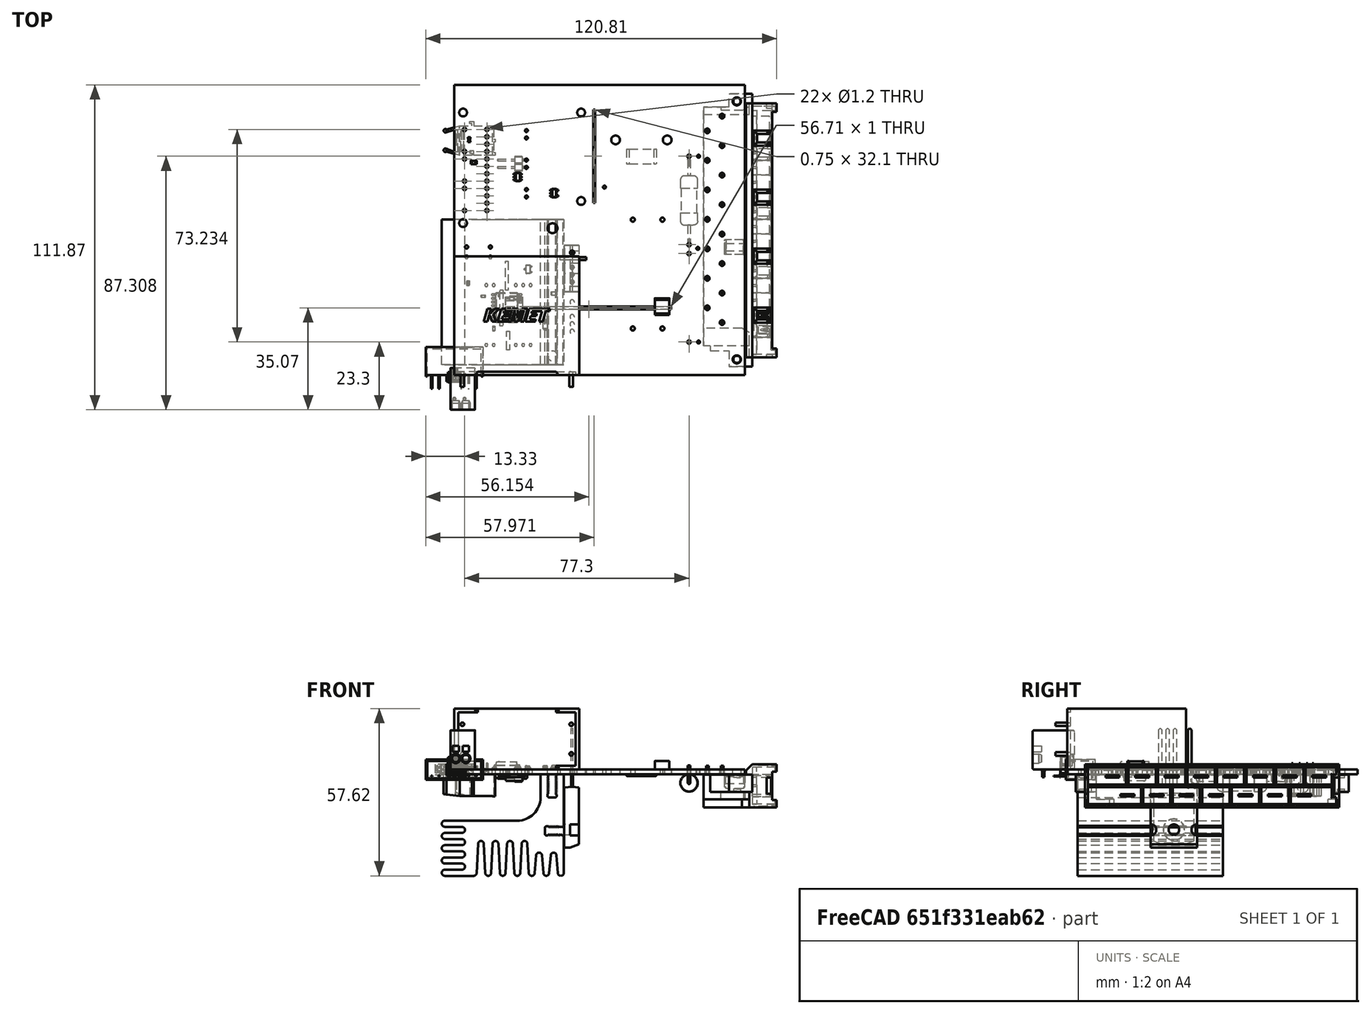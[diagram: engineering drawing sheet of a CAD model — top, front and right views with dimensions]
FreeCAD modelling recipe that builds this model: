
FCSTD DOCUMENT  (FreeCAD 1.0R39109 (Git))
Label: HalfBridge_SiC
License: All rights reserved
LicenseURL: https://en.wikipedia.org/wiki/All_rights_reserved
objects: App::Link×105, Part::Feature×46, App::Part×15, PartDesign::CoordinateSystem×1, Sketcher::SketchObject×1
note: 49 computed .brp shape members not serialized (recipe doc carries the construction recipe); baked Part::Feature solids carry a one-line shape summary decoded from their .brp

FEATURE [PartDesign::CoordinateSystem] Local_CS_ed05
  AttacherType = Attacher::AttachEngine3D
  MapMode = 2
FEATURE [Part::Feature] Pcb_ed05
  Placement = pos=(-39.5,140.5,0) rot=(0,0,1;0rad)
  shape: bbox 100 x 100 x 1.6 mm, 113 faces (baked)
FEATURE [Sketcher::SketchObject] PCB_Sketch_ed05
  ArcFitTolerance = 1e-06
  FullyConstrained = false
  MakeInternals = false
  sketch-geometry (28):
    g0: LineSegment StartX=17.542 StartY=39.29 StartZ=0 EndX=18.542 EndY=39.29 EndZ=0
    g1: LineSegment StartX=18.542 StartY=39.29 StartZ=0 EndX=18.542 EndY=29.29 EndZ=0
    g2: LineSegment StartX=18.542 StartY=29.29 StartZ=0 EndX=17.542 EndY=29.29 EndZ=0
    g3: LineSegment StartX=17.542 StartY=29.29 StartZ=0 EndX=17.542 EndY=39.29 EndZ=0
    g4: LineSegment StartX=36.399 StartY=40.662 StartZ=0 EndX=45.383 EndY=40.662 EndZ=0
    g5: LineSegment StartX=45.383 StartY=40.662 StartZ=0 EndX=45.383 EndY=39.662 EndZ=0
    g6: LineSegment StartX=45.383 StartY=39.662 StartZ=0 EndX=36.399 EndY=39.662 EndZ=0
    g7: LineSegment StartX=36.399 StartY=39.662 StartZ=0 EndX=36.399 EndY=40.662 EndZ=0
    g8: LineSegment StartX=47.768 StartY=91.487 StartZ=0 EndX=48.514 EndY=91.487 EndZ=0
    g9: LineSegment StartX=48.514 StartY=91.487 StartZ=0 EndX=48.514 EndY=59.389 EndZ=0
    g10: LineSegment StartX=48.514 StartY=59.389 StartZ=0 EndX=47.768 EndY=59.389 EndZ=0
    g11: LineSegment StartX=47.768 StartY=59.389 StartZ=0 EndX=47.768 EndY=91.487 EndZ=0
    g12: LineSegment StartX=17.968 StartY=23.7 StartZ=0 EndX=74.68 EndY=23.7 EndZ=0
    g13: LineSegment StartX=74.68 StartY=23.7 StartZ=0 EndX=74.68 EndY=22.7 EndZ=0
    g14: LineSegment StartX=74.68 StartY=22.7 StartZ=0 EndX=17.968 EndY=22.7 EndZ=0
    g15: LineSegment StartX=17.968 StartY=22.7 StartZ=0 EndX=17.968 EndY=23.7 EndZ=0
    g16: LineSegment StartX=0 StartY=100 StartZ=0 EndX=100 EndY=100 EndZ=0
    g17: LineSegment StartX=100 StartY=100 StartZ=0 EndX=100 EndY=0 EndZ=0
    g18: LineSegment StartX=100 StartY=0 StartZ=0 EndX=0 EndY=0 EndZ=0
    g19: LineSegment StartX=0 StartY=0 StartZ=0 EndX=0 EndY=100 EndZ=0
    g20: LineSegment StartX=18.05 StartY=15.208 StartZ=0 EndX=19.05 EndY=15.208 EndZ=0
    g21: LineSegment StartX=19.05 StartY=15.208 StartZ=0 EndX=19.05 EndY=8.7 EndZ=0
    g22: LineSegment StartX=19.05 StartY=8.7 StartZ=0 EndX=18.05 EndY=8.7 EndZ=0
    g23: LineSegment StartX=18.05 StartY=8.7 StartZ=0 EndX=18.05 EndY=15.208 EndZ=0
    g24: LineSegment StartX=15.764 StartY=29.4 StartZ=0 EndX=16.764 EndY=29.4 EndZ=0
    g25: LineSegment StartX=16.764 StartY=29.4 StartZ=0 EndX=16.764 EndY=16.9 EndZ=0
    g26: LineSegment StartX=16.764 StartY=16.9 StartZ=0 EndX=15.764 EndY=16.9 EndZ=0
    g27: LineSegment StartX=15.764 StartY=16.9 StartZ=0 EndX=15.764 EndY=29.4 EndZ=0
  constraints (28):
    c: Coincident(g18,g19)
    c: Coincident(g16,g19)
    c: Coincident(g26,g27)
    c: Coincident(g24,g27)
    c: Coincident(g25,g26)
    c: Coincident(g24,g25)
    c: Coincident(g2,g3)
    c: Coincident(g0,g3)
    c: Coincident(g14,g15)
    c: Coincident(g12,g15)
    c: Coincident(g22,g23)
    c: Coincident(g20,g23)
    c: Coincident(g1,g2)
    c: Coincident(g0,g1)
    c: Coincident(g21,g22)
    c: Coincident(g20,g21)
    c: Coincident(g6,g7)
    c: Coincident(g4,g7)
    c: Coincident(g5,g6)
    c: Coincident(g4,g5)
    c: Coincident(g10,g11)
    c: Coincident(g8,g11)
    c: Coincident(g9,g10)
    c: Coincident(g8,g9)
    c: Coincident(g13,g14)
    c: Coincident(g12,g13)
    c: Coincident(g17,g18)
    c: Coincident(g16,g17)
FEATURE [App::Part] Board_Geoms_ed05
  Group = -> [Pcb_ed05,PCB_Sketch_ed05]
  Origin = -> Origin
FEATURE [Part::Feature] Shape  label="U5_SOIC-16W_7.5x10.3mm_P1.27mm_noPin12_13_606f1c37d418"
  Placement = pos=(18,23.3,0) rot=(0,0,1;0rad)
  shape: bbox 10.3 x 10.3 x 2.75 mm, 256 faces (baked)
FEATURE [Part::Feature] Shape001  label="D6_D_SOD_123_86f777a7cf57"
  Placement = pos=(31.3,17.35,0) rot=(0,0,-1;1.5708rad)
  shape: bbox 1.6 x 3.8 x 1.25 mm, 67 faces (baked)
FEATURE [Part::Feature] Shape002  label="R9_R_0603_1608Metric_fe9d9f34c5f9"
  Placement = pos=(9.9875,27.2,0) rot=(0,0,1;0rad)
  shape: bbox 1.6 x 0.8 x 0.45 mm, 26 faces (baked)
FEATURE [App::Link] D6_D_SOD_123_86f777a7cf57_ln_  label="D5_D_SOD_123_75c73be4f775"
  LinkPlacement = pos=(31.3,29.9,0) rot=(0,0,1;1.5708rad)
  LinkedObject = -> Shape001
  Placement = pos=(31.3,29.9,0) rot=(0,0,1;1.5708rad)
FEATURE [Part::Feature] Shape003  label="C15_C_0603_1608Metric_09ddd0478757"
  Placement = pos=(13.5,16.1,0) rot=(0,0,-1;1.5708rad)
  shape: bbox 0.8 x 1.6 x 0.8 mm, 28 faces (baked)
FEATURE [App::Link] C15_C_0603_1608Metric_09ddd0478757_ln_  label="C33_C_0603_1608Metric_74bc470caa33"
  LinkPlacement = pos=(9.3,80.8715,0) rot=(0,0,1;1.5708rad)
  LinkedObject = -> Shape003
  Placement = pos=(9.3,80.8715,0) rot=(0,0,1;1.5708rad)
FEATURE [Part::Feature] Shape004  label="D3_LED_0603_1608Metric_70bb5031e2ff"
  Placement = pos=(4.7,31.775,0) rot=(0,0,-1;1.5708rad)
  shape: bbox 0.8 x 1.6 x 1.1 mm, 50 faces (baked)
FEATURE [Part::Feature] Shape005  label="C38_C_0805_2012Metric_74cbd35bff10"
  Placement = pos=(6.655,73.284,0) rot=(0,0,1;0rad)
  shape: bbox 2 x 1.25 x 1.25 mm, 28 faces (baked)
FEATURE [App::Link] R9_R_0603_1608Metric_fe9d9f34c5f9_ln_  label="R33_R_0603_1608Metric_ea8747869db3"
  LinkPlacement = pos=(22.7,83.4115,0) rot=(0,0,1;1.5708rad)
  LinkedObject = -> Shape002
  Placement = pos=(22.7,83.4115,0) rot=(0,0,1;1.5708rad)
FEATURE [App::Link] C15_C_0603_1608Metric_09ddd0478757_ln_001  label="C22_C_0603_1608Metric_3b7886544036"
  LinkPlacement = pos=(25.65,28.3,0) rot=(0,0,1;0rad)
  LinkedObject = -> Shape003
  Placement = pos=(25.65,28.3,0) rot=(0,0,1;0rad)
FEATURE [Part::Feature] Part__Feature  label="CAS_c_12B"
  Placement = pos=(0,-2.4,-3e-16) rot=(0,0,1;0rad)
  shape: bbox 5.4 x 2.5 x 4.2 mm, 71 faces (baked)
FEATURE [Part::Feature] Part__Feature001  label="1 pole_s"
  Placement = pos=(0.3,-0.6,-3e-16) rot=(0,0,1;0rad)
  shape: bbox 0.6 x 0.6 x 0.7 mm, 14 faces (baked)
FEATURE [App::Part] CAS_120B1  label="SW1_CAS-120B1_eba1f44a47b7[2]"
  Group = -> [Part__Feature,Part__Feature001]
  Origin = -> Origin008
  Placement = pos=(29.242,83.058,2.5) rot=(0.57735,-0.57735,-0.57735;2.0944rad)
FEATURE [App::Link] R9_R_0603_1608Metric_fe9d9f34c5f9_ln_001  label="R14_R_0603_1608Metric_f9b5c031c635"
  LinkPlacement = pos=(28.1,36.5,0) rot=(0,0,1;1.5708rad)
  LinkedObject = -> Shape002
  Placement = pos=(28.1,36.5,0) rot=(0,0,1;1.5708rad)
FEATURE [App::Link] R9_R_0603_1608Metric_fe9d9f34c5f9_ln_002  label="R8_R_0603_1608Metric_fcb6b5fbbfd0"
  LinkPlacement = pos=(10,28.7,0) rot=(0,0,1;0rad)
  LinkedObject = -> Shape002
  Placement = pos=(10,28.7,0) rot=(0,0,1;0rad)
FEATURE [App::Link] C15_C_0603_1608Metric_09ddd0478757_ln_002  label="C45_C_0603_1608Metric_6c9f5762c5a1"
  LinkPlacement = pos=(36.9,16.256,0) rot=(0,0,1;1.5708rad)
  LinkedObject = -> Shape003
  Placement = pos=(36.9,16.256,0) rot=(0,0,1;1.5708rad)
FEATURE [App::Link] C38_C_0805_2012Metric_74cbd35bff10_ln_  label="C24_C_0805_2012Metric_4c91d95a9eef"
  LinkPlacement = pos=(25.7,8.7,0) rot=(0,0,1;3.14159rad)
  LinkedObject = -> Shape005
  Placement = pos=(25.7,8.7,0) rot=(0,0,1;3.14159rad)
FEATURE [Part::Feature] Shape006  label="U10_SOT_23_6_8cf1dc40b667"
  Placement = pos=(21.85,68.3115,0) rot=(0,0,1;3.14159rad)
  shape: bbox 2.8 x 2.9 x 1.55 mm, 124 faces (baked)
FEATURE [App::Link] C15_C_0603_1608Metric_09ddd0478757_ln_003  label="C21_C_0603_1608Metric_d16c1e161e8d"
  LinkPlacement = pos=(25.62,18.5,0) rot=(0,0,1;3.14159rad)
  LinkedObject = -> Shape003
  Placement = pos=(25.62,18.5,0) rot=(0,0,1;3.14159rad)
FEATURE [App::Link] C15_C_0603_1608Metric_09ddd0478757_ln_004  label="C42_C_0603_1608Metric_20bf4b114d9d"
  LinkPlacement = pos=(25.1,68.1115,0) rot=(0,0,1;1.5708rad)
  LinkedObject = -> Shape003
  Placement = pos=(25.1,68.1115,0) rot=(0,0,1;1.5708rad)
FEATURE [App::Link] C38_C_0805_2012Metric_74cbd35bff10_ln_001  label="C18_C_0805_2012Metric_4df3bd6c3c50"
  LinkPlacement = pos=(25.7,33.1,0) rot=(0,0,1;3.14159rad)
  LinkedObject = -> Shape005
  Placement = pos=(25.7,33.1,0) rot=(0,0,1;3.14159rad)
FEATURE [App::Link] U10_SOT_23_6_8cf1dc40b667_ln_  label="U11_SOT_23_6_c211cb7acc4a"
  LinkPlacement = pos=(21.85,58.1515,0) rot=(0,0,1;3.14159rad)
  LinkedObject = -> Shape006
  Placement = pos=(21.85,58.1515,0) rot=(0,0,1;3.14159rad)
FEATURE [App::Link] R9_R_0603_1608Metric_fe9d9f34c5f9_ln_003  label="R15_R_0603_1608Metric_55e85660f00f"
  LinkPlacement = pos=(22.6,36.1,0) rot=(0,0,-1;1.5708rad)
  LinkedObject = -> Shape002
  Placement = pos=(22.6,36.1,0) rot=(0,0,-1;1.5708rad)
FEATURE [Part::Feature] Shape007  label="R21_R_0805_2012Metric_4eff570911b6"
  Placement = pos=(34.3,28.2,0) rot=(0,0,1;0rad)
  shape: bbox 2 x 1.2 x 0.45 mm, 26 faces (baked)
FEATURE [App::Link] C15_C_0603_1608Metric_09ddd0478757_ln_005  label="C34_C_0603_1608Metric_836b7f75df63"
  LinkPlacement = pos=(9.5,60.3715,0) rot=(0,0,1;1.5708rad)
  LinkedObject = -> Shape003
  Placement = pos=(9.5,60.3715,0) rot=(0,0,1;1.5708rad)
FEATURE [App::Link] C38_C_0805_2012Metric_74cbd35bff10_ln_002  label="C39_C_0805_2012Metric_4739b33e3560"
  LinkPlacement = pos=(6.655,83.9115,0) rot=(0,0,1;0rad)
  LinkedObject = -> Shape005
  Placement = pos=(6.655,83.9115,0) rot=(0,0,1;0rad)
FEATURE [App::Link] R9_R_0603_1608Metric_fe9d9f34c5f9_ln_004  label="R16_R_0603_1608Metric_5e29ad9bbd6c"
  LinkPlacement = pos=(29.7,13.3,0) rot=(0,0,-1;1.5708rad)
  LinkedObject = -> Shape002
  Placement = pos=(29.7,13.3,0) rot=(0,0,-1;1.5708rad)
FEATURE [App::Link] C15_C_0603_1608Metric_09ddd0478757_ln_006  label="C6_C_0603_1608Metric_47ec0beeeb7c"
  LinkPlacement = pos=(36.576,85.598,0) rot=(0,0,1;0rad)
  LinkedObject = -> Shape003
  Placement = pos=(36.576,85.598,0) rot=(0,0,1;0rad)
FEATURE [App::Link] D3_LED_0603_1608Metric_70bb5031e2ff_ln_  label="D1_LED_0603_1608Metric_117d22e4d741"
  LinkPlacement = pos=(3.1,9.525,0) rot=(0,0,1;1.5708rad)
  LinkedObject = -> Shape004
  Placement = pos=(3.1,9.525,0) rot=(0,0,1;1.5708rad)
FEATURE [Part::Feature] Shape008  label="U3_SOT_23_5_e32904241429"
  Placement = pos=(34.37,62.7015,0) rot=(0,0,1;0rad)
  shape: bbox 2.8 x 2.9 x 1.55 mm, 109 faces (baked)
FEATURE [App::Link] C38_C_0805_2012Metric_74cbd35bff10_ln_003  label="C35_C_0805_2012Metric_12818f10c88b"
  LinkPlacement = pos=(7.5,67.9115,0) rot=(0,0,1;3.14159rad)
  LinkedObject = -> Shape005
  Placement = pos=(7.5,67.9115,0) rot=(0,0,1;3.14159rad)
FEATURE [Part::Feature] Shape009  label="U7_SOT_23_ed8fd63cd947"
  Placement = pos=(25.3625,36.5,0) rot=(0,0,1;3.14159rad)
  shape: bbox 2.5 x 3 x 1.2 mm, 76 faces (baked)
FEATURE [Part::Feature] Shape010  label="C5_C_2220_5750Metric_40789e461117"
  Placement = pos=(71.498,23.622,0) rot=(0,0,-1;1.5708rad)
  shape: bbox 5 x 5.7 x 2.9 mm, 28 faces (baked)
FEATURE [App::Link] R9_R_0603_1608Metric_fe9d9f34c5f9_ln_005  label="R29_R_0603_1608Metric_c415b56a8a35"
  LinkPlacement = pos=(13.655,63.4115,0) rot=(0,0,1;1.5708rad)
  LinkedObject = -> Shape002
  Placement = pos=(13.655,63.4115,0) rot=(0,0,1;1.5708rad)
FEATURE [App::Link] R9_R_0603_1608Metric_fe9d9f34c5f9_ln_006  label="R27_R_0603_1608Metric_6ecdd8c441b3"
  LinkPlacement = pos=(13.3,73.9115,0) rot=(0,0,1;1.5708rad)
  LinkedObject = -> Shape002
  Placement = pos=(13.3,73.9115,0) rot=(0,0,1;1.5708rad)
FEATURE [App::Link] R9_R_0603_1608Metric_fe9d9f34c5f9_ln_007  label="R30_R_0603_1608Metric_3d9fcfb98980"
  LinkPlacement = pos=(18.7,78.4115,0) rot=(0,0,1;1.5708rad)
  LinkedObject = -> Shape002
  Placement = pos=(18.7,78.4115,0) rot=(0,0,1;1.5708rad)
FEATURE [App::Link] C15_C_0603_1608Metric_09ddd0478757_ln_007  label="C41_C_0603_1608Metric_8a3fc6cb6ce4"
  LinkPlacement = pos=(25.1,78.4115,0) rot=(0,0,1;1.5708rad)
  LinkedObject = -> Shape003
  Placement = pos=(25.1,78.4115,0) rot=(0,0,1;1.5708rad)
FEATURE [App::Link] C5_C_2220_5750Metric_40789e461117_ln_  label="C3_C_2220_5750Metric_0b14797a19db"
  LinkPlacement = pos=(59.498,23.622,0) rot=(0,0,-1;1.5708rad)
  LinkedObject = -> Shape010
  Placement = pos=(59.498,23.622,0) rot=(0,0,-1;1.5708rad)
FEATURE [App::Link] R21_R_0805_2012Metric_4eff570911b6_ln_  label="R19_R_0805_2012Metric_5467f9f4486e"
  LinkPlacement = pos=(34.3,32.2,0) rot=(0,0,1;0rad)
  LinkedObject = -> Shape007
  Placement = pos=(34.3,32.2,0) rot=(0,0,1;0rad)
FEATURE [App::Link] C15_C_0603_1608Metric_09ddd0478757_ln_008  label="C43_C_0603_1608Metric_b35c248b52c4"
  LinkPlacement = pos=(25.1,58.1115,0) rot=(0,0,1;1.5708rad)
  LinkedObject = -> Shape003
  Placement = pos=(25.1,58.1115,0) rot=(0,0,1;1.5708rad)
FEATURE [App::Link] R21_R_0805_2012Metric_4eff570911b6_ln_001  label="R3_R_0805_2012Metric_ab16afa742b3"
  LinkPlacement = pos=(44.564,16.278,0) rot=(0,0,1;1.5708rad)
  LinkedObject = -> Shape007
  Placement = pos=(44.564,16.278,0) rot=(0,0,1;1.5708rad)
FEATURE [App::Link] R21_R_0805_2012Metric_4eff570911b6_ln_002  label="R10_R_0805_2012Metric_e1b373d5c9e0"
  LinkPlacement = pos=(8.1,18.67,0) rot=(0,0,-1;1.5708rad)
  LinkedObject = -> Shape007
  Placement = pos=(8.1,18.67,0) rot=(0,0,-1;1.5708rad)
FEATURE [App::Link] D3_LED_0603_1608Metric_70bb5031e2ff_ln_001  label="D2_LED_0603_1608Metric_72f350e39bfe"
  LinkPlacement = pos=(4.7,35.5,0) rot=(0,0,-1;1.5708rad)
  LinkedObject = -> Shape004
  Placement = pos=(4.7,35.5,0) rot=(0,0,-1;1.5708rad)
FEATURE [App::Link] R9_R_0603_1608Metric_fe9d9f34c5f9_ln_008  label="R32_R_0603_1608Metric_bd0168379d35"
  LinkPlacement = pos=(18.7,58.1115,0) rot=(0,0,1;1.5708rad)
  LinkedObject = -> Shape002
  Placement = pos=(18.7,58.1115,0) rot=(0,0,1;1.5708rad)
FEATURE [App::Link] C38_C_0805_2012Metric_74cbd35bff10_ln_004  label="C40_C_0805_2012Metric_1a8242036e69"
  LinkPlacement = pos=(6.7,63.1115,0) rot=(0,0,1;0rad)
  LinkedObject = -> Shape005
  Placement = pos=(6.7,63.1115,0) rot=(0,0,1;0rad)
FEATURE [App::Link] R21_R_0805_2012Metric_4eff570911b6_ln_003  label="R40_R_0805_2012Metric_1fb8d6502ab2"
  LinkPlacement = pos=(20.574,16.04,0) rot=(0,0,-1;1.5708rad)
  LinkedObject = -> Shape007
  Placement = pos=(20.574,16.04,0) rot=(0,0,-1;1.5708rad)
FEATURE [App::Link] C15_C_0603_1608Metric_09ddd0478757_ln_009  label="C20_C_0603_1608Metric_5de1c2e82c4e"
  LinkPlacement = pos=(25.62,21.1,0) rot=(0,0,1;0rad)
  LinkedObject = -> Shape003
  Placement = pos=(25.62,21.1,0) rot=(0,0,1;0rad)
FEATURE [App::Link] R9_R_0603_1608Metric_fe9d9f34c5f9_ln_009  label="R28_R_0603_1608Metric_db2da8ac741f"
  LinkPlacement = pos=(13.3,84.0715,0) rot=(0,0,1;1.5708rad)
  LinkedObject = -> Shape002
  Placement = pos=(13.3,84.0715,0) rot=(0,0,1;1.5708rad)
FEATURE [App::Link] C38_C_0805_2012Metric_74cbd35bff10_ln_005  label="C25_C_0805_2012Metric_d4570dd2b406"
  LinkPlacement = pos=(21.9,8.7,0) rot=(0,0,1;3.14159rad)
  LinkedObject = -> Shape005
  Placement = pos=(21.9,8.7,0) rot=(0,0,1;3.14159rad)
FEATURE [Part::Feature] Shape011  label="L5_L_0603_1608Metric_90973c27a168"
  Placement = pos=(5.1,81.1115,0) rot=(0,0,1;1.5708rad)
  shape: bbox 0.8 x 1.6 x 0.8 mm, 28 faces (baked)
FEATURE [App::Link] R21_R_0805_2012Metric_4eff570911b6_ln_004  label="R26_R_0805_2012Metric_215f856b24f5"
  LinkPlacement = pos=(34.3,13.9,0) rot=(0,0,1;0rad)
  LinkedObject = -> Shape007
  Placement = pos=(34.3,13.9,0) rot=(0,0,1;0rad)
FEATURE [App::Link] L5_L_0603_1608Metric_90973c27a168_ln_  label="L6_L_0603_1608Metric_227bb48d5cae"
  LinkPlacement = pos=(5.1,60.4265,0) rot=(0,0,1;1.5708rad)
  LinkedObject = -> Shape011
  Placement = pos=(5.1,60.4265,0) rot=(0,0,1;1.5708rad)
FEATURE [App::Link] C15_C_0603_1608Metric_09ddd0478757_ln_010  label="C14_C_0603_1608Metric_a25fa12fbfe8"
  LinkPlacement = pos=(11.3,24.6,0) rot=(0,0,-1;1.5708rad)
  LinkedObject = -> Shape003
  Placement = pos=(11.3,24.6,0) rot=(0,0,-1;1.5708rad)
FEATURE [App::Link] R9_R_0603_1608Metric_fe9d9f34c5f9_ln_010  label="R31_R_0603_1608Metric_1647f0dc400e"
  LinkPlacement = pos=(18.7,68.3115,0) rot=(0,0,1;1.5708rad)
  LinkedObject = -> Shape002
  Placement = pos=(18.7,68.3115,0) rot=(0,0,1;1.5708rad)
FEATURE [App::Link] C38_C_0805_2012Metric_74cbd35bff10_ln_006  label="C37_C_0805_2012Metric_821d07cd279f"
  LinkPlacement = pos=(7.5,57.7115,0) rot=(0,0,1;3.14159rad)
  LinkedObject = -> Shape005
  Placement = pos=(7.5,57.7115,0) rot=(0,0,1;3.14159rad)
FEATURE [App::Link] C5_C_2220_5750Metric_40789e461117_ln_001  label="C4_C_2220_5750Metric_aeb9c5b40f04"
  LinkPlacement = pos=(65.498,23.622,0) rot=(0,0,-1;1.5708rad)
  LinkedObject = -> Shape010
  Placement = pos=(65.498,23.622,0) rot=(0,0,-1;1.5708rad)
FEATURE [Part::Feature] Part__Feature002  label="CAS_c_D2B"
  Placement = pos=(0,-2.4,-3e-16) rot=(0,0,1;0rad)
  shape: bbox 5.4 x 2.5 x 5.6 mm, 110 faces (baked)
FEATURE [Part::Feature] Part__Feature003  label="Dual_s"
  Placement = pos=(0.3,-0.6,0.64) rot=(0,0,1;0rad)
  shape: bbox 0.6 x 0.6 x 0.7 mm, 14 faces (baked)
FEATURE [Part::Feature] Part__Feature004  label="Dual_s001"
  Placement = pos=(0.3,-0.6,-0.64) rot=(0,0,1;0rad)
  shape: bbox 0.6 x 0.6 x 0.7 mm, 14 faces (baked)
FEATURE [App::Part] CAS_D20B1  label="SW5_CAS-D20B1_b4c165cab9b4[2]"
  Group = -> [Part__Feature002,Part__Feature003,Part__Feature004]
  Origin = -> Origin009
  Placement = pos=(4.29,22.754,2.5) rot=(0,0.707107,0.707107;3.14159rad)
FEATURE [App::Link] R9_R_0603_1608Metric_fe9d9f34c5f9_ln_011  label="R35_R_0603_1608Metric_3c432ada0ca8"
  LinkPlacement = pos=(22.7,72.9115,0) rot=(0,0,1;1.5708rad)
  LinkedObject = -> Shape002
  Placement = pos=(22.7,72.9115,0) rot=(0,0,1;1.5708rad)
FEATURE [App::Link] U7_SOT_23_ed8fd63cd947_ln_  label="U8_SOT_23_df60fcb6f98c"
  LinkPlacement = pos=(25.3625,13.6,0) rot=(0,0,1;3.14159rad)
  LinkedObject = -> Shape009
  Placement = pos=(25.3625,13.6,0) rot=(0,0,1;3.14159rad)
FEATURE [App::Link] L5_L_0603_1608Metric_90973c27a168_ln_001  label="L4_L_0603_1608Metric_8fa15f76ae30"
  LinkPlacement = pos=(5.1,70.5865,0) rot=(0,0,1;1.5708rad)
  LinkedObject = -> Shape011
  Placement = pos=(5.1,70.5865,0) rot=(0,0,1;1.5708rad)
FEATURE [App::Link] SW1_CAS_120B1_eba1f44a47b7_2__ln_  label="SW3_CAS-120B1_d768a4589788[2]"
  LinkPlacement = pos=(29.21,62.484,2.5) rot=(0.57735,-0.57735,-0.57735;2.0944rad)
  LinkedObject = -> CAS_120B1
  Placement = pos=(29.21,62.484,2.5) rot=(0.57735,-0.57735,-0.57735;2.0944rad)
FEATURE [App::Link] C15_C_0603_1608Metric_09ddd0478757_ln_011  label="C32_C_0603_1608Metric_89b2b6ef811b"
  LinkPlacement = pos=(9.3,70.7115,0) rot=(0,0,1;1.5708rad)
  LinkedObject = -> Shape003
  Placement = pos=(9.3,70.7115,0) rot=(0,0,1;1.5708rad)
FEATURE [App::Link] C38_C_0805_2012Metric_74cbd35bff10_ln_007  label="C36_C_0805_2012Metric_4e65c6641553"
  LinkPlacement = pos=(7.9,78.1115,0) rot=(0,0,1;3.14159rad)
  LinkedObject = -> Shape005
  Placement = pos=(7.9,78.1115,0) rot=(0,0,1;3.14159rad)
FEATURE [App::Link] C5_C_2220_5750Metric_40789e461117_ln_002  label="C2_C_2220_5750Metric_dfcbf9cf85c4"
  LinkPlacement = pos=(53.498,23.622,0) rot=(0,0,-1;1.5708rad)
  LinkedObject = -> Shape010
  Placement = pos=(53.498,23.622,0) rot=(0,0,-1;1.5708rad)
FEATURE [App::Link] C15_C_0603_1608Metric_09ddd0478757_ln_012  label="C23_C_0603_1608Metric_094c659e187e"
  LinkPlacement = pos=(25.65,25.3,0) rot=(0,0,1;3.14159rad)
  LinkedObject = -> Shape003
  Placement = pos=(25.65,25.3,0) rot=(0,0,1;3.14159rad)
FEATURE [App::Link] R21_R_0805_2012Metric_4eff570911b6_ln_005  label="R20_R_0805_2012Metric_ea78c8c8eecd"
  LinkPlacement = pos=(34.3,30.2,0) rot=(0,0,1;0rad)
  LinkedObject = -> Shape007
  Placement = pos=(34.3,30.2,0) rot=(0,0,1;0rad)
FEATURE [App::Link] C38_C_0805_2012Metric_74cbd35bff10_ln_008  label="C16_C_0805_2012Metric_e5af641f3413"
  LinkPlacement = pos=(12.5,33.7,0) rot=(0,0,1;0rad)
  LinkedObject = -> Shape005
  Placement = pos=(12.5,33.7,0) rot=(0,0,1;0rad)
FEATURE [App::Link] R9_R_0603_1608Metric_fe9d9f34c5f9_ln_012  label="R34_R_0603_1608Metric_211ac095cb09"
  LinkPlacement = pos=(22.7,63.1115,0) rot=(0,0,1;1.5708rad)
  LinkedObject = -> Shape002
  Placement = pos=(22.7,63.1115,0) rot=(0,0,1;1.5708rad)
FEATURE [App::Link] C15_C_0603_1608Metric_09ddd0478757_ln_013  label="C27_C_0603_1608Metric_298082643862"
  LinkPlacement = pos=(23.6375,16.1,0) rot=(0,0,1;3.14159rad)
  LinkedObject = -> Shape003
  Placement = pos=(23.6375,16.1,0) rot=(0,0,1;3.14159rad)
FEATURE [App::Link] R21_R_0805_2012Metric_4eff570911b6_ln_006  label="R2_R_0805_2012Metric_96e20fc01cb7"
  LinkPlacement = pos=(44.564,33.296,0) rot=(0,0,1;1.5708rad)
  LinkedObject = -> Shape007
  Placement = pos=(44.564,33.296,0) rot=(0,0,1;1.5708rad)
FEATURE [App::Link] R9_R_0603_1608Metric_fe9d9f34c5f9_ln_013  label="R13_R_0603_1608Metric_df329fa1d19c"
  LinkPlacement = pos=(29.7,36.5,0) rot=(0,0,-1;1.5708rad)
  LinkedObject = -> Shape002
  Placement = pos=(29.7,36.5,0) rot=(0,0,-1;1.5708rad)
FEATURE [App::Link] U3_SOT_23_5_e32904241429_ln_  label="U2_SOT_23_5_6f2eb00efaad"
  LinkPlacement = pos=(34.37,72.8615,0) rot=(0,0,1;0rad)
  LinkedObject = -> Shape008
  Placement = pos=(34.37,72.8615,0) rot=(0,0,1;0rad)
FEATURE [App::Link] L5_L_0603_1608Metric_90973c27a168_ln_002  label="L2_L_0603_1608Metric_6584b5c4d191"
  LinkPlacement = pos=(9.3,33.1,0) rot=(0,0,-1;1.5708rad)
  LinkedObject = -> Shape011
  Placement = pos=(9.3,33.1,0) rot=(0,0,-1;1.5708rad)
FEATURE [App::Link] L5_L_0603_1608Metric_90973c27a168_ln_003  label="L3_L_0603_1608Metric_80e3bdf1ad67"
  LinkPlacement = pos=(9.3,8.7,0) rot=(0,0,1;1.5708rad)
  LinkedObject = -> Shape011
  Placement = pos=(9.3,8.7,0) rot=(0,0,1;1.5708rad)
FEATURE [App::Link] R21_R_0805_2012Metric_4eff570911b6_ln_007  label="R23_R_0805_2012Metric_772e2aabec3d"
  LinkPlacement = pos=(34.3,19.85,0) rot=(0,0,1;0rad)
  LinkedObject = -> Shape007
  Placement = pos=(34.3,19.85,0) rot=(0,0,1;0rad)
FEATURE [App::Link] C38_C_0805_2012Metric_74cbd35bff10_ln_009  label="C17_C_0805_2012Metric_9d67934c64c5"
  LinkPlacement = pos=(12.1,8.1,0) rot=(0,0,1;0rad)
  LinkedObject = -> Shape005
  Placement = pos=(12.1,8.1,0) rot=(0,0,1;0rad)
FEATURE [App::Link] U10_SOT_23_6_8cf1dc40b667_ln_001  label="U9_SOT_23_6_77935cb89beb"
  LinkPlacement = pos=(21.85,78.4715,0) rot=(0,0,1;3.14159rad)
  LinkedObject = -> Shape006
  Placement = pos=(21.85,78.4715,0) rot=(0,0,1;3.14159rad)
FEATURE [App::Link] C38_C_0805_2012Metric_74cbd35bff10_ln_010  label="C19_C_0805_2012Metric_f233b5c27be5"
  LinkPlacement = pos=(21.9,33.1,0) rot=(0,0,1;3.14159rad)
  LinkedObject = -> Shape005
  Placement = pos=(21.9,33.1,0) rot=(0,0,1;3.14159rad)
FEATURE [App::Link] SW1_CAS_120B1_eba1f44a47b7_2__ln_001  label="SW2_CAS-120B1_de4e8c04cc20[2]"
  LinkPlacement = pos=(29.242,72.898,2.5) rot=(0.57735,-0.57735,-0.57735;2.0944rad)
  LinkedObject = -> CAS_120B1
  Placement = pos=(29.242,72.898,2.5) rot=(0.57735,-0.57735,-0.57735;2.0944rad)
FEATURE [App::Link] R21_R_0805_2012Metric_4eff570911b6_ln_008  label="R25_R_0805_2012Metric_61226d1b2b79"
  LinkPlacement = pos=(34.3,15.9,0) rot=(0,0,1;0rad)
  LinkedObject = -> Shape007
  Placement = pos=(34.3,15.9,0) rot=(0,0,1;0rad)
FEATURE [App::Link] C15_C_0603_1608Metric_09ddd0478757_ln_014  label="C8_C_0603_1608Metric_fd007361b396"
  LinkPlacement = pos=(36.322,65.278,0) rot=(0,0,1;0rad)
  LinkedObject = -> Shape003
  Placement = pos=(36.322,65.278,0) rot=(0,0,1;0rad)
FEATURE [App::Link] C15_C_0603_1608Metric_09ddd0478757_ln_015  label="C7_C_0603_1608Metric_2aaeb20b4386"
  LinkPlacement = pos=(36.4755,75.438,0) rot=(0,0,1;0rad)
  LinkedObject = -> Shape003
  Placement = pos=(36.4755,75.438,0) rot=(0,0,1;0rad)
FEATURE [App::Link] C15_C_0603_1608Metric_09ddd0478757_ln_016  label="C26_C_0603_1608Metric_365ecaa62ea9"
  LinkPlacement = pos=(23.7,38.95,0) rot=(0,0,1;3.14159rad)
  LinkedObject = -> Shape003
  Placement = pos=(23.7,38.95,0) rot=(0,0,1;3.14159rad)
FEATURE [App::Link] C15_C_0603_1608Metric_09ddd0478757_ln_017  label="C11_C_0603_1608Metric_54b4a60d9175"
  LinkPlacement = pos=(10.2875,21.3,0) rot=(0,0,1;3.14159rad)
  LinkedObject = -> Shape003
  Placement = pos=(10.2875,21.3,0) rot=(0,0,1;3.14159rad)
FEATURE [App::Link] R21_R_0805_2012Metric_4eff570911b6_ln_009  label="R24_R_0805_2012Metric_5be639e06338"
  LinkPlacement = pos=(34.3,17.9,0) rot=(0,0,1;0rad)
  LinkedObject = -> Shape007
  Placement = pos=(34.3,17.9,0) rot=(0,0,1;0rad)
FEATURE [App::Link] SW5_CAS_D20B1_b4c165cab9b4_2__ln_  label="SW4_CAS-D20B1_eed64a9be6db[2]"
  LinkPlacement = pos=(4.29,15.168,2.5) rot=(0,0.707107,0.707107;3.14159rad)
  LinkedObject = -> CAS_D20B1
  Placement = pos=(4.29,15.168,2.5) rot=(0,0.707107,0.707107;3.14159rad)
FEATURE [App::Link] R9_R_0603_1608Metric_fe9d9f34c5f9_ln_014  label="R17_R_0603_1608Metric_026225098221"
  LinkPlacement = pos=(28.1,13.3,0) rot=(0,0,1;1.5708rad)
  LinkedObject = -> Shape002
  Placement = pos=(28.1,13.3,0) rot=(0,0,1;1.5708rad)
FEATURE [App::Link] D3_LED_0603_1608Metric_70bb5031e2ff_ln_002  label="D4_LED_0603_1608Metric_dc75b572683f"
  LinkPlacement = pos=(4.7,28.175,0) rot=(0,0,-1;1.5708rad)
  LinkedObject = -> Shape004
  Placement = pos=(4.7,28.175,0) rot=(0,0,-1;1.5708rad)
FEATURE [App::Link] C15_C_0603_1608Metric_09ddd0478757_ln_018  label="C44_C_0603_1608Metric_1898ed5e7091"
  LinkPlacement = pos=(36.9,33.02,0) rot=(0,0,1;1.5708rad)
  LinkedObject = -> Shape003
  Placement = pos=(36.9,33.02,0) rot=(0,0,1;1.5708rad)
FEATURE [App::Link] R21_R_0805_2012Metric_4eff570911b6_ln_010  label="R22_R_0805_2012Metric_455d99f14320"
  LinkPlacement = pos=(34.3,26.2,0) rot=(0,0,1;0rad)
  LinkedObject = -> Shape007
  Placement = pos=(34.3,26.2,0) rot=(0,0,1;0rad)
FEATURE [App::Link] R9_R_0603_1608Metric_fe9d9f34c5f9_ln_015  label="R18_R_0603_1608Metric_e5275256b3fe"
  LinkPlacement = pos=(22.7,13.246,0) rot=(0,0,-1;1.5708rad)
  LinkedObject = -> Shape002
  Placement = pos=(22.7,13.246,0) rot=(0,0,-1;1.5708rad)
FEATURE [App::Link] U3_SOT_23_5_e32904241429_ln_001  label="U1_SOT_23_5_8fc5e1a9f18e"
  LinkPlacement = pos=(34.37,83.0215,0) rot=(0,0,1;0rad)
  LinkedObject = -> Shape008
  Placement = pos=(34.37,83.0215,0) rot=(0,0,1;0rad)
FEATURE [App::Part] Top_ed05
  Group = -> [Shape,Shape001,Shape002,D6_D_SOD_123_86f777a7cf57_ln_,Shape003,C15_C_0603_1608Metric_09ddd0478757_ln_,Shape004,Shape005,R9_R_0603_1608Metric_fe9d9f34c5f9_ln_,C15_C_0603_1608Metric_09ddd0478757_ln_001,CAS_120B1,R9_R_0603_1608Metric_fe9d9f34c5f9_ln_001,R9_R_0603_1608Metric_fe9d9f34c5f9_ln_002,C15_C_0603_1608Metric_09ddd0478757_ln_002,C38_C_0805_2012Metric_74cbd35bff10_ln_,Shape006,+74 more]
  Origin = -> Origin003
FEATURE [Part::Feature] Shape012  label="R36_R_Axial_DIN0617_L170mm_D60mm_P3048mm_Horizontal_e9082eb0809f"
  Placement = pos=(80.8,75.438,-1.6) rot=(0.707107,-0.707107,0;3.14159rad)
  shape: bbox 6.494 x 31.54 x 9.247 mm, 17 faces (baked)
FEATURE [App::Link] C38_C_0805_2012Metric_74cbd35bff10_ln_011  label="C30_C_0805_2012Metric_99b0a26469c9"
  LinkPlacement = pos=(25.8,20.7,-1.6) rot=(1,0,0;3.14159rad)
  LinkedObject = -> Shape005
  Placement = pos=(25.8,20.7,-1.6) rot=(1,0,0;3.14159rad)
FEATURE [App::Link] C15_C_0603_1608Metric_09ddd0478757_ln_019  label="C10_C_0603_1608Metric_a9055c7e1f35"
  LinkPlacement = pos=(10,27.2,-1.6) rot=(0,1,0;3.14159rad)
  LinkedObject = -> Shape003
  Placement = pos=(10,27.2,-1.6) rot=(0,1,0;3.14159rad)
FEATURE [App::Link] C38_C_0805_2012Metric_74cbd35bff10_ln_012  label="C12_C_0805_2012Metric_7a36f4b334d7"
  LinkPlacement = pos=(4.7,23.5,-1.6) rot=(0.707107,0.707107,0;3.14159rad)
  LinkedObject = -> Shape005
  Placement = pos=(4.7,23.5,-1.6) rot=(0.707107,0.707107,0;3.14159rad)
FEATURE [Part::Feature] Shape013  label="J4_Broadcom_AFBR-16xxZ_Horizontal_9b6c4e7f7e3c"
  Placement = pos=(11.2,84.664,-1.6) rot=(0,1,0;3.14159rad)
  shape: bbox 17.71 x 11.7 x 11.4 mm, 100 faces (baked)
FEATURE [App::Link] R21_R_0805_2012Metric_4eff570911b6_ln_011  label="R11_R_0805_2012Metric_904fb74af206"
  LinkPlacement = pos=(23.492,38.646,-1.6) rot=(1,0,0;3.14159rad)
  LinkedObject = -> Shape007
  Placement = pos=(23.492,38.646,-1.6) rot=(1,0,0;3.14159rad)
FEATURE [Part::Feature] Part__Feature005  label="79fa9e9c-a09d-11ed-8f45-a0cec80452fd_part"
  shape: bbox 8.4 x 14.4 x 13.5 mm, 26 faces (baked)
FEATURE [App::Part] _9fa9e9c_a09d_11ed_8f45_a0cec80452fd  label="79fa9e9c-a09d-11ed-8f45-a0cec80452fd"
  Group = -> [Part__Feature005]
  Origin = -> Origin010
FEATURE [Part::Feature] Part__Feature006  label="79faa16c-a09d-11ed-8f45-a0cec80452fd_part"
  shape: bbox 1.1 x 1.1 x 2.6 mm, 12 faces (baked)
FEATURE [Part::Feature] Part__Feature007  label="79faa16c-a09d-11ed-8f45-a0cec80452fd_part001"
  shape: bbox 1.1 x 1.1 x 2.6 mm, 12 faces (baked)
FEATURE [Part::Feature] Part__Feature008  label="79faa16c-a09d-11ed-8f45-a0cec80452fd_part002"
  shape: bbox 1.1 x 1.1 x 2.6 mm, 12 faces (baked)
FEATURE [Part::Feature] Part__Feature009  label="79faa16c-a09d-11ed-8f45-a0cec80452fd_part003"
  shape: bbox 1.1 x 1.1 x 2.6 mm, 12 faces (baked)
FEATURE [App::Part] _9faa16c_a09d_11ed_8f45_a0cec80452fd_part  label="79faa16c-a09d-11ed-8f45-a0cec80452fd_part004"
  Group = -> [Part__Feature006,Part__Feature007,Part__Feature008,Part__Feature009]
  Origin = -> Origin011
FEATURE [App::Part] _9faa16c_a09d_11ed_8f45_a0cec80452fd  label="79faa16c-a09d-11ed-8f45-a0cec80452fd"
  Group = -> [_9faa16c_a09d_11ed_8f45_a0cec80452fd_part]
  Origin = -> Origin012
FEATURE [App::Part] _9fa99c4_a09d_11ed_8f45_a0cec80452fd  label="79fa99c4-a09d-11ed-8f45-a0cec80452fd"
  Group = -> [_9fa9e9c_a09d_11ed_8f45_a0cec80452fd,_9faa16c_a09d_11ed_8f45_a0cec80452fd]
  Origin = -> Origin013
FEATURE [App::Part] CQ_assembly  label="J1_CQ assembly_c40872800de1"
  Group = -> [_9fa99c4_a09d_11ed_8f45_a0cec80452fd]
  Origin = -> Origin014
  Placement = pos=(12.4,40.678,-1.6) rot=(0.707107,0.707107,0;3.14159rad)
FEATURE [Part::Feature] Shape014  label="J10_PinHeader_1x02_P254mm_Horizontal_7643f22ec726"
  Placement = pos=(24.8,74.1115,-1.6) rot=(0,1,0;3.14159rad)
  shape: bbox 10.36 x 5.08 x 5.54 mm, 58 faces (baked)
FEATURE [App::Link] C38_C_0805_2012Metric_74cbd35bff10_ln_013  label="C28_C_0805_2012Metric_76606bb4505c"
  LinkPlacement = pos=(25.8,28.232,-1.6) rot=(1,0,0;3.14159rad)
  LinkedObject = -> Shape005
  Placement = pos=(25.8,28.232,-1.6) rot=(1,0,0;3.14159rad)
FEATURE [Part::Feature] Shape015  label="J2_C-413638-E_37cd69765024[2]"
  Placement = pos=(110.98,49.92,-5.6) rot=(0.57735,-0.57735,0.57735;4.18879rad)
  shape: bbox 25.2 x 94 x 14.8 mm, 484 faces (baked)
FEATURE [App::Link] R9_R_0603_1608Metric_fe9d9f34c5f9_ln_016  label="R4_R_0603_1608Metric_d5e5e0a8c182"
  LinkPlacement = pos=(3.875,35.5,-1.6) rot=(0.707107,-0.707107,0;3.14159rad)
  LinkedObject = -> Shape002
  Placement = pos=(3.875,35.5,-1.6) rot=(0.707107,-0.707107,0;3.14159rad)
FEATURE [App::Link] R9_R_0603_1608Metric_fe9d9f34c5f9_ln_017  label="R1_R_0603_1608Metric_12d23797164c"
  LinkPlacement = pos=(4.1,9.525,-1.6) rot=(0.707107,0.707107,0;3.14159rad)
  LinkedObject = -> Shape002
  Placement = pos=(4.1,9.525,-1.6) rot=(0.707107,0.707107,0;3.14159rad)
FEATURE [App::Link] J10_PinHeader_1x02_P254mm_Horizontal_7643f22ec726_ln_  label="J11_PinHeader_1x02_P254mm_Horizontal_fc1500a1b926"
  LinkPlacement = pos=(24.8,63.9515,-1.6) rot=(0,1,0;3.14159rad)
  LinkedObject = -> Shape014
  Placement = pos=(24.8,63.9515,-1.6) rot=(0,1,0;3.14159rad)
FEATURE [Part::Feature] Shape016  label="J13_1_cfcac89c0bd5[2]"
  Placement = pos=(96.5,44.12,-1.6) rot=(0.707107,-0.707107,0;3.14159rad)
  shape: bbox 7 x 4.98 x 4.98 mm, 13 faces (baked)
FEATURE [Part::Feature] Shape017  label="R39_R_4020_10251Metric_6d765f65bd79"
  Placement = pos=(64.4,75.4,-1.6) rot=(1,0,0;3.14159rad)
  shape: bbox 10.2 x 5.1 x 0.6 mm, 26 faces (baked)
FEATURE [Part::Feature] Part__Feature010  label="T1T1M-02-T-SH-L"
  Placement = pos=(0,0,0) rot=(1,0,0;1.5708rad)
  shape: bbox 4.4 x 4.6 x 5.2 mm, 86 faces (baked)
FEATURE [Part::Feature] Part__Feature011  label="P2T1M-02-F-SH-L"
  Placement = pos=(0,0,0) rot=(1,0,0;1.5708rad)
  shape: bbox 1.2 x 2.22 x 1.2 mm, 19 faces (baked)
FEATURE [Part::Feature] Part__Feature012  label="P22T1M-02-F-SH-L"
  Placement = pos=(0,0,0) rot=(1,0,0;1.5708rad)
  shape: bbox 1.2 x 0.4 x 3.971 mm, 15 faces (baked)
FEATURE [App::Part] T1M_02_F_SH_L  label="J6_T1M-02-F-SH-L_0a7fe3b67a9c[2]"
  Group = -> [Part__Feature010,Part__Feature011,Part__Feature012]
  Origin = -> Origin015
  Placement = pos=(31.4,67.734,-3.98) rot=(0.57735,0.57735,-0.57735;4.18879rad)
FEATURE [Part::Feature] Shape018  label="HS1_sk687_9ae714bd8fdf[2]"
  Placement = pos=(33.982,3.642,-1.55) rot=(0,0.707107,-0.707107;3.14159rad)
  shape: bbox 42 x 50 x 35 mm, 258 faces (baked)
FEATURE [App::Link] J6_T1M_02_F_SH_L_0a7fe3b67a9c_2__ln_  label="J7_T1M-02-F-SH-L_7059b7eb8092[2]"
  LinkPlacement = pos=(31.4,77.894,-3.98) rot=(0.57735,0.57735,-0.57735;4.18879rad)
  LinkedObject = -> T1M_02_F_SH_L
  Placement = pos=(31.4,77.894,-3.98) rot=(0.57735,0.57735,-0.57735;4.18879rad)
FEATURE [App::Link] R39_R_4020_10251Metric_6d765f65bd79_ln_  label="R38_R_4020_10251Metric_23694b22d5d4"
  LinkPlacement = pos=(64.4,81.2,-1.6) rot=(1,0,0;3.14159rad)
  LinkedObject = -> Shape017
  Placement = pos=(64.4,81.2,-1.6) rot=(1,0,0;3.14159rad)
FEATURE [App::Link] C38_C_0805_2012Metric_74cbd35bff10_ln_014  label="C13_C_0805_2012Metric_5e4ca477a655"
  LinkPlacement = pos=(9.9,21.7,-1.6) rot=(1,0,0;3.14159rad)
  LinkedObject = -> Shape005
  Placement = pos=(9.9,21.7,-1.6) rot=(1,0,0;3.14159rad)
FEATURE [App::Link] J10_PinHeader_1x02_P254mm_Horizontal_7643f22ec726_ln_001  label="J9_PinHeader_1x02_P254mm_Horizontal_9237b5c6f450"
  LinkPlacement = pos=(24.8,84.2715,-1.6) rot=(0,1,0;3.14159rad)
  LinkedObject = -> Shape014
  Placement = pos=(24.8,84.2715,-1.6) rot=(0,1,0;3.14159rad)
FEATURE [App::Link] R9_R_0603_1608Metric_fe9d9f34c5f9_ln_018  label="R5_R_0603_1608Metric_697492a11508"
  LinkPlacement = pos=(3.875,31.775,-1.6) rot=(0.707107,-0.707107,0;3.14159rad)
  LinkedObject = -> Shape002
  Placement = pos=(3.875,31.775,-1.6) rot=(0.707107,-0.707107,0;3.14159rad)
FEATURE [App::Link] J4_Broadcom_AFBR_16xxZ_Horizontal_9b6c4e7f7e3c_ln_  label="J5_Broadcom_AFBR-16xxZ_Horizontal_cc90251d43e9"
  LinkPlacement = pos=(11.2,64.344,-1.6) rot=(0,1,0;3.14159rad)
  LinkedObject = -> Shape013
  Placement = pos=(11.2,64.344,-1.6) rot=(0,1,0;3.14159rad)
FEATURE [App::Link] C15_C_0603_1608Metric_09ddd0478757_ln_020  label="C9_C_0603_1608Metric_8758c5b1e71b"
  LinkPlacement = pos=(10,28.7,-1.6) rot=(0,1,0;3.14159rad)
  LinkedObject = -> Shape003
  Placement = pos=(10,28.7,-1.6) rot=(0,1,0;3.14159rad)
FEATURE [App::Link] R9_R_0603_1608Metric_fe9d9f34c5f9_ln_019  label="R7_R_0603_1608Metric_6e0015b41d89"
  LinkPlacement = pos=(2.9,24.5,-1.6) rot=(0.707107,-0.707107,0;3.14159rad)
  LinkedObject = -> Shape002
  Placement = pos=(2.9,24.5,-1.6) rot=(0.707107,-0.707107,0;3.14159rad)
FEATURE [Part::Feature] Part__Feature013  label="CFP_RB4_42X40X20_L43H41T21S37.5S110.2LL4F1.25"
  shape: bbox 43 x 45 x 21 mm, 30 faces (baked)
FEATURE [Part::Feature] Part__Feature014  label="CFP_RB4_42X40X20_L43H41T21S37.5S110.2LL4F1.026"
  shape: bbox 8.475 x 4.477 x 0.005 mm, 19 faces (baked)
FEATURE [Part::Feature] Part__Feature015  label="CFP_RB4_42X40X20_L43H41T21S37.5S110.2LL4F1.027"
  shape: bbox 10.33 x 4.477 x 0.005 mm, 25 faces (baked)
FEATURE [Part::Feature] Part__Feature016  label="CFP_RB4_42X40X20_L43H41T21S37.5S110.2LL4F1.028"
  shape: bbox 5.39 x 4.477 x 0.005 mm, 13 faces (baked)
FEATURE [App::Part] CFP_RB4_42X40X20_L43H41T21S37_5S110_2LL4F1_25  label="C1_CFP_RB4_42X40X20_L43H41T21S37.5S110.2LL4F1.029_59f146c23d11[2]"
  Group = -> [Part__Feature013,Part__Feature014,Part__Feature015,Part__Feature016]
  Origin = -> Origin016
  Placement = pos=(56.028,56.336,-1.6) rot=(0.57735,-0.57735,0.57735;4.18879rad)
FEATURE [Part::Feature] Shape019  label="Q1_TO-247-4_Vertical_4070ae466a86"
  Placement = pos=(40.55,42.209,-1.6) rot=(0.707107,-0.707107,0;3.14159rad)
  shape: bbox 5.03 x 15.9 x 41.1 mm, 74 faces (baked)
FEATURE [App::Link] J13_1_cfcac89c0bd5_2__ln_  label="J14_1_45c35c22a121[2]"
  LinkPlacement = pos=(96.5,64.44,-1.6) rot=(0.707107,-0.707107,0;3.14159rad)
  LinkedObject = -> Shape016
  Placement = pos=(96.5,64.44,-1.6) rot=(0.707107,-0.707107,0;3.14159rad)
FEATURE [Part::Feature] Part__Feature017  label="RKZ-xx2005D_case"
  shape: bbox 19.65 x 10.2 x 7.05 mm, 112 faces (baked)
FEATURE [Part::Feature] Part__Feature018  label="RKZ-xx2005D_pin1(+Vin)"
  shape: bbox 0.5 x 4.6 x 0.25 mm, 6 faces (baked)
FEATURE [Part::Feature] Part__Feature019  label="RKZ-xx2005D_pin7(+Vout)"
  shape: bbox 0.5 x 4.6 x 0.25 mm, 6 faces (baked)
FEATURE [Part::Feature] Part__Feature020  label="RKZ-xx2005D_pin5(-Vout)"
  shape: bbox 0.5 x 4.6 x 0.25 mm, 6 faces (baked)
FEATURE [Part::Feature] Part__Feature021  label="RKZ-xx2005D_pin6(Com)"
  shape: bbox 0.5 x 4.6 x 0.25 mm, 6 faces (baked)
FEATURE [Part::Feature] Part__Feature022  label="RKZ-xx2005D_pin2(-Vin)"
  shape: bbox 0.5 x 4.6 x 0.25 mm, 6 faces (baked)
FEATURE [Part::Feature] Part__Feature023  label="RKZ-xx2005D_potting"
  shape: bbox 18.55 x 8.95 x 6 mm, 6 faces (baked)
FEATURE [App::Part] RKZ_xx2005D  label="U6_RKZ_xx2005D_0645041a10aa[2]"
  Group = -> [Part__Feature017,Part__Feature018,Part__Feature019,Part__Feature020,Part__Feature021,Part__Feature022,Part__Feature023]
  Origin = -> Origin017
  Placement = pos=(18.85,12.664,-1.6) rot=(-1,0,0;1.5708rad)
FEATURE [App::Link] U6_RKZ_xx2005D_0645041a10aa_2__ln_  label="U4_RKZ_xx2005D_740929d25b34[2]"
  LinkPlacement = pos=(18.85,33.276,-1.6) rot=(-1,0,0;1.5708rad)
  LinkedObject = -> RKZ_xx2005D
  Placement = pos=(18.85,33.276,-1.6) rot=(-1,0,0;1.5708rad)
FEATURE [App::Link] J6_T1M_02_F_SH_L_0a7fe3b67a9c_2__ln_001  label="J8_T1M-02-F-SH-L_f87a2e85d4db[2]"
  LinkPlacement = pos=(31.4,57.574,-3.98) rot=(0.57735,0.57735,-0.57735;4.18879rad)
  LinkedObject = -> T1M_02_F_SH_L
  Placement = pos=(31.4,57.574,-3.98) rot=(0.57735,0.57735,-0.57735;4.18879rad)
FEATURE [App::Link] Q1_TO_247_4_Vertical_4070ae466a86_ln_  label="Q2_TO-247-4_Vertical_c7c841d41241"
  LinkPlacement = pos=(40.55,25.209,-1.6) rot=(0.707107,-0.707107,0;3.14159rad)
  LinkedObject = -> Shape019
  Placement = pos=(40.55,25.209,-1.6) rot=(0.707107,-0.707107,0;3.14159rad)
FEATURE [App::Link] C38_C_0805_2012Metric_74cbd35bff10_ln_015  label="C29_C_0805_2012Metric_ea01a7009c54"
  LinkPlacement = pos=(25.7995,25.692,-1.6) rot=(0,1,0;3.14159rad)
  LinkedObject = -> Shape005
  Placement = pos=(25.7995,25.692,-1.6) rot=(0,1,0;3.14159rad)
FEATURE [App::Link] L5_L_0603_1608Metric_90973c27a168_ln_004  label="L1_L_0603_1608Metric_e9d47b7cc21e"
  LinkPlacement = pos=(7.375,23.5,-1.6) rot=(1,0,0;3.14159rad)
  LinkedObject = -> Shape011
  Placement = pos=(7.375,23.5,-1.6) rot=(1,0,0;3.14159rad)
FEATURE [App::Link] R21_R_0805_2012Metric_4eff570911b6_ln_012  label="R12_R_0805_2012Metric_000eced81897"
  LinkPlacement = pos=(24.892,7.874,-1.6) rot=(1,0,0;3.14159rad)
  LinkedObject = -> Shape007
  Placement = pos=(24.892,7.874,-1.6) rot=(1,0,0;3.14159rad)
FEATURE [App::Link] R9_R_0603_1608Metric_fe9d9f34c5f9_ln_020  label="R6_R_0603_1608Metric_4e81408e4251"
  LinkPlacement = pos=(3.9,28.175,-1.6) rot=(0.707107,-0.707107,0;3.14159rad)
  LinkedObject = -> Shape002
  Placement = pos=(3.9,28.175,-1.6) rot=(0.707107,-0.707107,0;3.14159rad)
FEATURE [App::Link] R36_R_Axial_DIN0617_L170mm_D60mm_P3048mm_Horizontal_e9082eb0809f_ln_  label="R37_R_Axial_DIN0617_L170mm_D60mm_P3048mm_Horizontal_4fcf1ba42225"
  LinkPlacement = pos=(80.8,41.91,-1.6) rot=(0.707107,-0.707107,0;3.14159rad)
  LinkedObject = -> Shape012
  Placement = pos=(80.8,41.91,-1.6) rot=(0.707107,-0.707107,0;3.14159rad)
FEATURE [App::Link] J13_1_cfcac89c0bd5_2__ln_001  label="J12_1_5d39db0f3e7c[2]"
  LinkPlacement = pos=(96.5,23.8,-1.6) rot=(0.707107,-0.707107,0;3.14159rad)
  LinkedObject = -> Shape016
  Placement = pos=(96.5,23.8,-1.6) rot=(0.707107,-0.707107,0;3.14159rad)
FEATURE [App::Link] J13_1_cfcac89c0bd5_2__ln_002  label="J15_1_77f750f6aa21[2]"
  LinkPlacement = pos=(96.5,84.76,-1.6) rot=(0.707107,-0.707107,0;3.14159rad)
  LinkedObject = -> Shape016
  Placement = pos=(96.5,84.76,-1.6) rot=(0.707107,-0.707107,0;3.14159rad)
FEATURE [App::Link] C38_C_0805_2012Metric_74cbd35bff10_ln_016  label="C31_C_0805_2012Metric_a2a63c8358cd"
  LinkPlacement = pos=(25.8,18.7,-1.6) rot=(0,1,0;3.14159rad)
  LinkedObject = -> Shape005
  Placement = pos=(25.8,18.7,-1.6) rot=(0,1,0;3.14159rad)
FEATURE [Part::Feature] Shape020  label="D7_D_SMC_a35920f9d814"
  Placement = pos=(20.55,23.216,-1.6) rot=(0.707107,-0.707107,0;3.14159rad)
  shape: bbox 5.9 x 8 x 2.31 mm, 41 faces (baked)
FEATURE [App::Link] J4_Broadcom_AFBR_16xxZ_Horizontal_9b6c4e7f7e3c_ln_001  label="J3_Broadcom_AFBR-16xxZ_Horizontal_92a701fb3616"
  LinkPlacement = pos=(11.2,74.504,-1.6) rot=(0,1,0;3.14159rad)
  LinkedObject = -> Shape013
  Placement = pos=(11.2,74.504,-1.6) rot=(0,1,0;3.14159rad)
FEATURE [App::Part] Bot_ed05
  Group = -> [Shape012,C38_C_0805_2012Metric_74cbd35bff10_ln_011,C15_C_0603_1608Metric_09ddd0478757_ln_019,C38_C_0805_2012Metric_74cbd35bff10_ln_012,Shape013,R21_R_0805_2012Metric_4eff570911b6_ln_011,CQ_assembly,Shape014,C38_C_0805_2012Metric_74cbd35bff10_ln_013,Shape015,R9_R_0603_1608Metric_fe9d9f34c5f9_ln_016,R9_R_0603_1608Metric_fe9d9f34c5f9_ln_017,J10_PinHeader_1x02_P254mm_Horizontal_7643f22ec726_ln_,+29 more]
  Origin = -> Origin004
FEATURE [App::Part] Step_Models_ed05
  Group = -> [Top_ed05,Bot_ed05]
  Origin = -> Origin002
FEATURE [App::Part] Board_ed05  label="HalfBridge_SiC"
  Group = -> [Local_CS_ed05,Board_Geoms_ed05,Step_Models_ed05]
  Origin = -> Origin001
